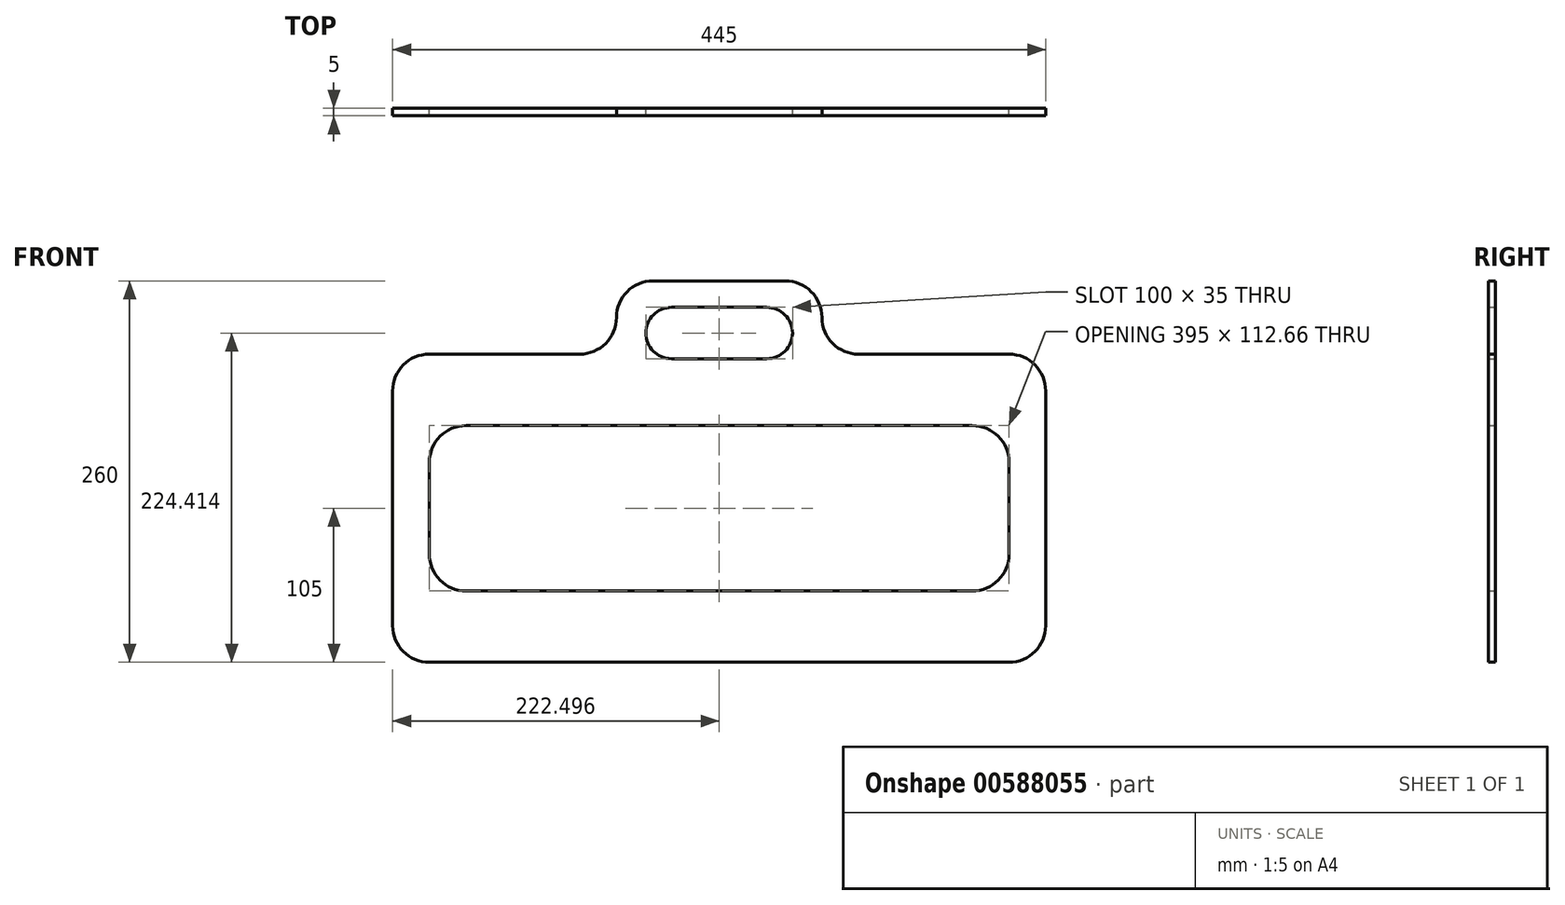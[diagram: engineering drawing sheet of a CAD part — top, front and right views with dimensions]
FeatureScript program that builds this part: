
annotation { "Feature Type Name" : "Feature", "Feature Type Description" : "" }
export const myFeature = defineFeature(function(context is Context, id is Id, definition is map)
    precondition{}
    {
        {
            var Q0;
            Q0=qCreatedBy(makeId("Front.planeOp"),FACE);
            var sketch = newSketch(context, id + "F0", { "sketchPlane" : qUnion([Q0])});
            skLineSegment(sketch, "E0.left", {"start": v(-122.26, 121.19) * mm, "end": v(-122.26, 118.69) * mm, "construction": true});
            skLineSegment(sketch, "E1", {"start": v(-122.26, 121.19) * mm, "end": v(322.74, -41.47) * mm, "construction": true});
            skLineSegment(sketch, "E2", {"start": v(322.74, 121.19) * mm, "end": v(-122.26, -40.14) * mm, "construction": true});
            skLineSegment(sketch, "E3.bottom", {"start": v(-97.26, 144.86) * mm, "end": v(5.24, 144.86) * mm});
            skLineSegment(sketch, "E3.left", {"start": v(-122.26, 121.19) * mm, "end": v(-122.26, 119.86) * mm});
            skPoint(sketch, "E3.middle", {"position": v(100.24, 39.86) * mm});
            skLineSegment(sketch, "E4.trimOffspring", {"start": v(-122.26, -40.14) * mm, "end": v(-122.26, -40.14) * mm});
            skPoint(sketch, "E5.visualSharp", {"position": v(-122.26, -65.14) * mm});
            skArc(sketch, "E5.filletArc", {"start": v(-122.26, -40.14) * mm, "mid": v(-114.94, -57.82) * mm, "end": v(-97.26, -65.14) * mm});
            skPoint(sketch, "E6.visualSharp", {"position": v(-122.26, 144.86) * mm});
            skArc(sketch, "E6.filletArc", {"start": v(-97.26, 144.86) * mm, "mid": v(-114.94, 137.54) * mm, "end": v(-122.26, 119.86) * mm});
            skPoint(sketch, "E7.visualSharp", {"position": v(322.74, 144.86) * mm});
            skPoint(sketch, "E8.visualSharp", {"position": v(322.74, -65.14) * mm});
            skLineSegment(sketch, "E9.bottom", {"start": v(297.74, 144.86) * mm, "end": v(195.24, 144.86) * mm});
            skLineSegment(sketch, "E9.top", {"start": v(145.24, 194.86) * mm, "end": v(55.24, 194.86) * mm});
            skLineSegment(sketch, "E10.left", {"start": v(170.24, 169.86) * mm, "end": v(170.24, 169.86) * mm});
            skLineSegment(sketch, "E10.right", {"start": v(30.24, 169.86) * mm, "end": v(30.24, 169.86) * mm});
            skPoint(sketch, "E10.middle", {"position": v(100.24, 169.86) * mm});
            skPoint(sketch, "E11.orphan", {"position": v(-122.26, 194.86) * mm});
            skPoint(sketch, "E9.left.end.orphan", {"position": v(322.74, 194.86) * mm});
            skLineSegment(sketch, "E12.trimOffspring", {"start": v(195.24, 144.86) * mm, "end": v(297.74, 144.86) * mm});
            skLineSegment(sketch, "E13.trimOffspring", {"start": v(5.24, 144.86) * mm, "end": v(-97.26, 144.86) * mm});
            skPoint(sketch, "E14.visualSharp", {"position": v(30.24, 144.86) * mm});
            skArc(sketch, "E14.filletArc", {"start": v(5.24, 144.86) * mm, "mid": v(22.91, 152.18) * mm, "end": v(30.24, 169.86) * mm});
            skPoint(sketch, "E15.visualSharp", {"position": v(30.24, 194.86) * mm});
            skArc(sketch, "E15.filletArc", {"start": v(55.24, 194.86) * mm, "mid": v(37.56, 187.54) * mm, "end": v(30.24, 169.86) * mm});
            skPoint(sketch, "E16.visualSharp", {"position": v(170.24, 194.86) * mm});
            skArc(sketch, "E16.filletArc", {"start": v(170.24, 169.86) * mm, "mid": v(162.91, 187.54) * mm, "end": v(145.24, 194.86) * mm});
            skPoint(sketch, "E17.visualSharp", {"position": v(170.24, 144.86) * mm});
            skArc(sketch, "E17.filletArc", {"start": v(170.24, 169.86) * mm, "mid": v(177.56, 152.18) * mm, "end": v(195.24, 144.86) * mm});
            skPoint(sketch, "E18.middle", {"position": v(100.24, 121.19) * mm});
            skPoint(sketch, "E19.middle", {"position": v(100.24, -40.8) * mm});
            skPoint(sketch, "E20.orphan", {"position": v(322.74, 123.69) * mm});
            skLineSegment(sketch, "E21.trimOffspring", {"start": v(100.24, 121.19) * mm, "end": v(322.74, 121.19) * mm, "construction": true});
            skPoint(sketch, "E22.trimOffspring.end.orphan", {"position": v(-122.26, -37.64) * mm});
            skPoint(sketch, "E23.trimOffspring.end.orphan", {"position": v(-122.26, -43.97) * mm});
            skPoint(sketch, "E24.trimOffspring.end.orphan", {"position": v(-122.26, 118.69) * mm});
            skPoint(sketch, "E25.trimOffspring.end.orphan", {"position": v(-122.26, 123.69) * mm});
            skPoint(sketch, "E26.orphan", {"position": v(322.74, -43.97) * mm});
            skLineSegment(sketch, "E27.trimOffspring", {"start": v(-122.26, -37.64) * mm, "end": v(-122.26, -40.14) * mm, "construction": true});
            skLineSegment(sketch, "E28.trimOffspring", {"start": v(100.24, -40.8) * mm, "end": v(322.74, -41.47) * mm, "construction": true});
            skLineSegment(sketch, "E29", {"start": v(-97.26, -65.14) * mm, "end": v(297.74, -65.14) * mm});
            skPoint(sketch, "E30.orphan", {"position": v(100.24, 144.86) * mm});
            skPoint(sketch, "E31.start.orphan", {"position": v(100.24, 194.86) * mm});
            skLineSegment(sketch, "E32", {"start": v(100.24, 194.86) * mm, "end": v(100.24, 123.69) * mm, "construction": true});
            skLineSegment(sketch, "E33.bottom", {"start": v(132.74, 141.77) * mm, "end": v(67.74, 141.77) * mm});
            skLineSegment(sketch, "E33.top", {"start": v(132.74, 176.77) * mm, "end": v(67.74, 176.77) * mm});
            skLineSegment(sketch, "E33.left", {"start": v(150.24, 159.27) * mm, "end": v(150.24, 159.27) * mm});
            skLineSegment(sketch, "E33.right", {"start": v(50.24, 159.27) * mm, "end": v(50.24, 159.27) * mm});
            skPoint(sketch, "E33.middle", {"position": v(100.24, 159.27) * mm});
            skPoint(sketch, "E34.visualSharp", {"position": v(50.24, 176.77) * mm});
            skArc(sketch, "E34.filletArc", {"start": v(67.74, 176.77) * mm, "mid": v(55.36, 171.65) * mm, "end": v(50.24, 159.27) * mm});
            skPoint(sketch, "E35.visualSharp", {"position": v(150.24, 176.77) * mm});
            skArc(sketch, "E35.filletArc", {"start": v(150.24, 159.27) * mm, "mid": v(145.1, 171.65) * mm, "end": v(132.74, 176.77) * mm});
            skPoint(sketch, "E36.visualSharp", {"position": v(150.24, 141.77) * mm});
            skArc(sketch, "E36.filletArc", {"start": v(132.74, 141.77) * mm, "mid": v(145.1, 146.9) * mm, "end": v(150.24, 159.27) * mm});
            skPoint(sketch, "E37.visualSharp", {"position": v(50.24, 141.77) * mm});
            skArc(sketch, "E37.filletArc", {"start": v(50.24, 159.27) * mm, "mid": v(55.36, 146.9) * mm, "end": v(67.74, 141.77) * mm});
            skPoint(sketch, "E38.orphan", {"position": v(100.24, -37.64) * mm});
            skPoint(sketch, "E39.end.orphan", {"position": v(100.24, -43.97) * mm});
            skPoint(sketch, "E40.start.orphan", {"position": v(100.24, 118.69) * mm});
            skLineSegment(sketch, "E41", {"start": v(-122.26, 121.19) * mm, "end": v(-122.26, -40.14) * mm});
            skLineSegment(sketch, "E42.bottom", {"start": v(-72.26, 96.19) * mm, "end": v(272.74, 96.19) * mm});
            skLineSegment(sketch, "E42.top", {"start": v(-72.26, -16.47) * mm, "end": v(272.74, -16.47) * mm});
            skLineSegment(sketch, "E42.left", {"start": v(-97.26, 71.19) * mm, "end": v(-97.26, 8.53) * mm});
            skLineSegment(sketch, "E42.right", {"start": v(297.74, 71.19) * mm, "end": v(297.74, 8.53) * mm});
            skPoint(sketch, "E43.visualSharp", {"position": v(-97.26, 96.19) * mm});
            skArc(sketch, "E43.filletArc", {"start": v(-72.26, 96.19) * mm, "mid": v(-89.94, 88.87) * mm, "end": v(-97.26, 71.19) * mm});
            skPoint(sketch, "E44.visualSharp", {"position": v(-97.26, -16.47) * mm});
            skArc(sketch, "E44.filletArc", {"start": v(-97.26, 8.53) * mm, "mid": v(-89.94, -9.15) * mm, "end": v(-72.26, -16.47) * mm});
            skPoint(sketch, "E45.visualSharp", {"position": v(297.74, -16.47) * mm});
            skArc(sketch, "E45.filletArc", {"start": v(272.74, -16.47) * mm, "mid": v(290.41, -9.15) * mm, "end": v(297.74, 8.53) * mm});
            skPoint(sketch, "E46.visualSharp", {"position": v(297.74, 96.19) * mm});
            skArc(sketch, "E46.filletArc", {"start": v(297.74, 71.19) * mm, "mid": v(290.41, 88.87) * mm, "end": v(272.74, 96.19) * mm});
            skPoint(sketch, "E8.filletArc.end.orphan", {"position": v(322.61, -42.64) * mm});
            skPoint(sketch, "E3.right.start.orphan", {"position": v(322.74, 118.69) * mm});
            skPoint(sketch, "E47.orphan", {"position": v(322.74, -37.64) * mm});
            skPoint(sketch, "E48.end.orphan", {"position": v(322.74, -42.64) * mm});
            skLineSegment(sketch, "E49", {"start": v(322.74, 119.86) * mm, "end": v(322.74, -40.14) * mm});
            skLineSegment(sketch, "E50", {"start": v(297.74, -65.14) * mm, "end": v(297.74, -65.14) * mm});
            skLineSegment(sketch, "E51", {"start": v(297.74, 144.86) * mm, "end": v(297.74, 144.86) * mm});
            skArc(sketch, "E52.filletArc", {"start": v(322.74, 119.86) * mm, "mid": v(315.41, 137.54) * mm, "end": v(297.74, 144.86) * mm});
            skArc(sketch, "E53.filletArc", {"start": v(297.74, -65.14) * mm, "mid": v(315.41, -57.82) * mm, "end": v(322.74, -40.14) * mm});
            skSolve(sketch);
        }
        {
            var Q0;
            Q0 = qSketchRegion(id + "F0", true);
            extrude(context, id + "F1", {"entities" : qUnion([Q0]), "depth" : 5 * mm, "offsetDistance" : 25 * mm});
        }
    });
